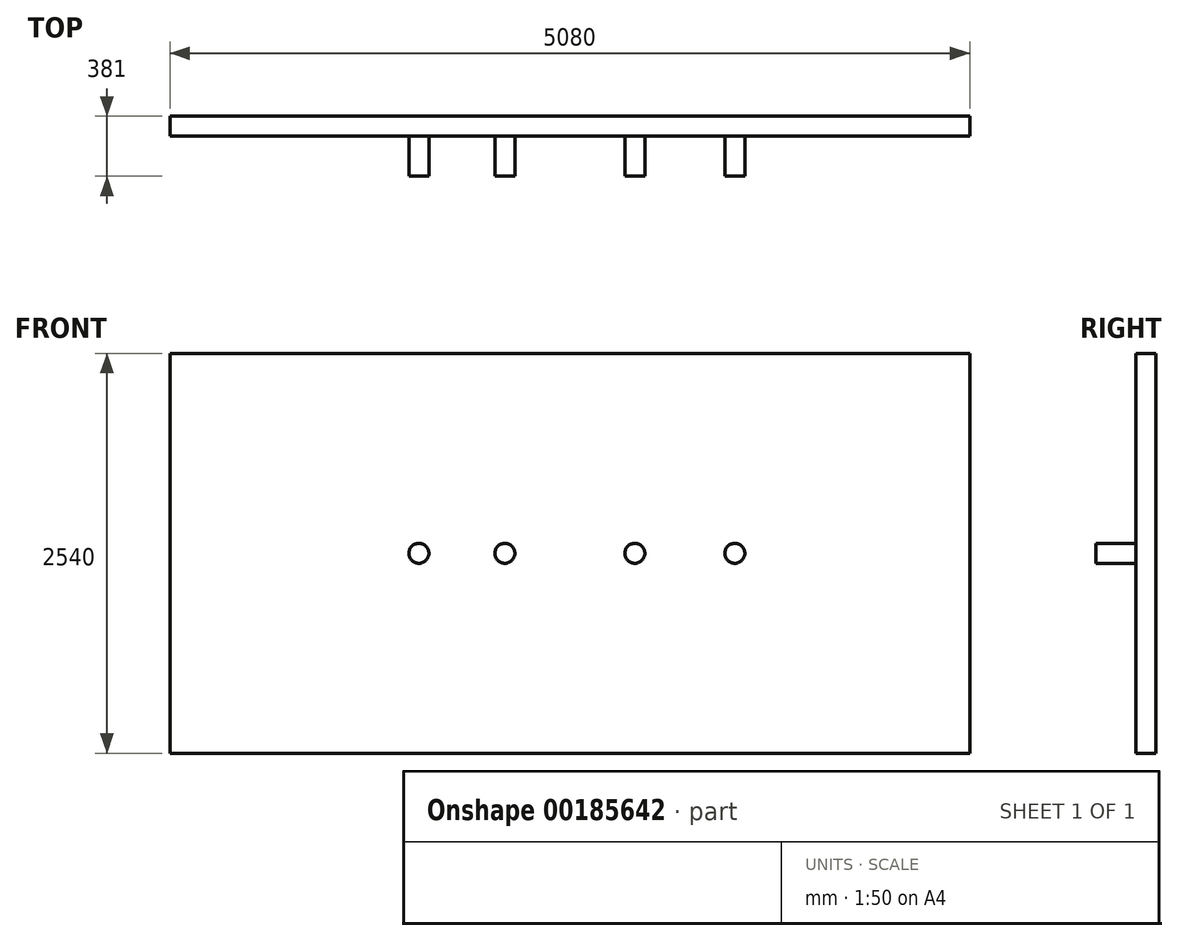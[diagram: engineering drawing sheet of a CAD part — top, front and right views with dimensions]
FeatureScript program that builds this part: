
annotation { "Feature Type Name" : "Feature", "Feature Type Description" : "" }
export const myFeature = defineFeature(function(context is Context, id is Id, definition is map)
    precondition{}
    {
        {
            var Q0;
            Q0=qCreatedBy(makeId("Front.planeOp"),FACE);
            var sketch = newSketch(context, id + "F0", { "sketchPlane" : qUnion([Q0])});
            skLineSegment(sketch, "E0.bottom", {"start": v(2540, 1270) * mm, "end": v(-2540, 1270) * mm});
            skLineSegment(sketch, "E0.top", {"start": v(2540, -1270) * mm, "end": v(-2540, -1270) * mm});
            skLineSegment(sketch, "E0.left", {"start": v(2540, 1270) * mm, "end": v(2540, -1270) * mm});
            skLineSegment(sketch, "E0.right", {"start": v(-2540, 1270) * mm, "end": v(-2540, -1270) * mm});
            skSolve(sketch);
        }
        {
            var Q0;
            Q0 = qSketchRegion(id + "F0", true);
            extrude(context, id + "F1", {"entities" : qUnion([Q0]), "depth" : 127 * mm});
        }
        {
            var Q0;
            Q0=makeQuery(id+"F1.opExtrude","CAP_FACE",FACE,{"disambiguationData":[OSD([sQuery(id+"F0.wireOp",EDGE,"E0.bottom"),sQuery(id+"F0.wireOp",EDGE,"E0.top"),sQuery(id+"F0.wireOp",EDGE,"E0.left"),sQuery(id+"F0.wireOp",EDGE,"E0.right")])],"isStart":false});
            var sketch = newSketch(context, id + "F2", { "sketchPlane" : qUnion([Q0])});
            skCircle(sketch, "E1", {"center": v(-958.85, 0) * mm, "radius": 63.5 * mm});
            skCircle(sketch, "E2", {"center": v(-412.75, 0) * mm, "radius": 63.5 * mm});
            skCircle(sketch, "E3", {"center": v(412.75, 0) * mm, "radius": 63.5 * mm});
            skCircle(sketch, "E4", {"center": v(1047.75, 0) * mm, "radius": 63.5 * mm});
            skLineSegment(sketch, "E5", {"start": v(0, 0) * mm, "end": v(0, 1151.28) * mm, "construction": true});
            skLineSegment(sketch, "E6", {"start": v(0, 0) * mm, "end": v(-2055.6, 0) * mm, "construction": true});
            skSolve(sketch);
        }
        {
            var Q0;
            Q0 = qSketchRegion(id + "F2", true);
            extrude(context, id + "F3", {"entities" : qUnion([Q0]), "operationType" : NewBodyOperationType.ADD, "depth" : 254 * mm});
        }
    });
